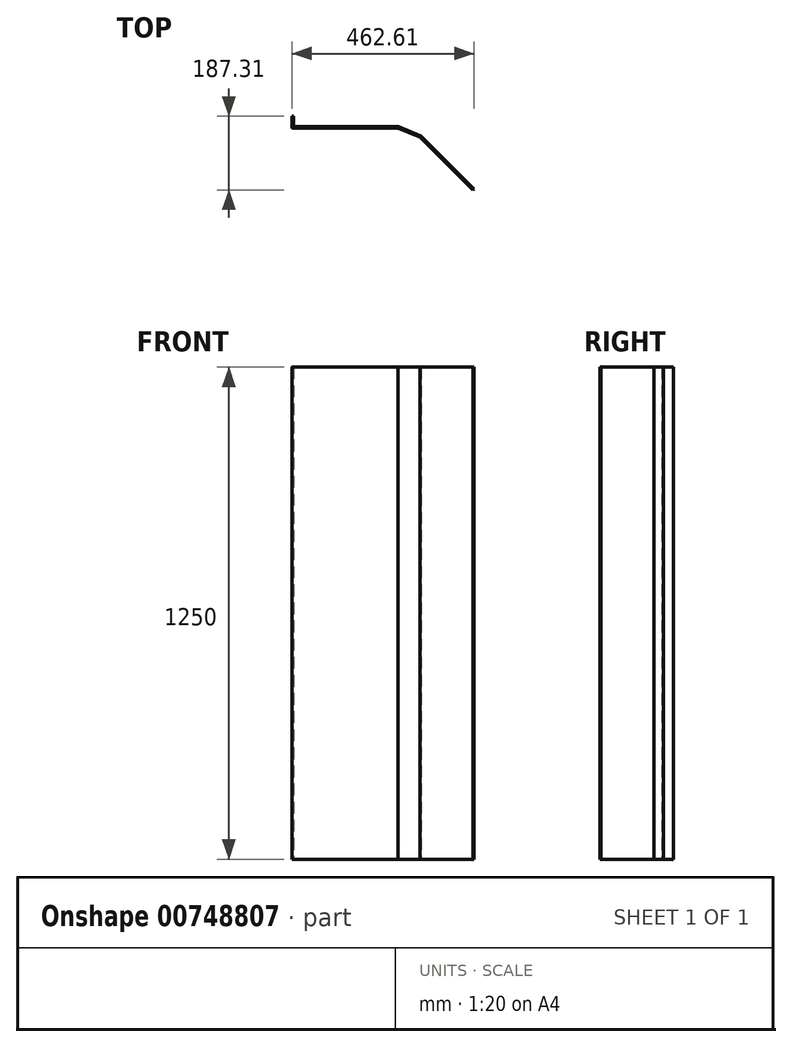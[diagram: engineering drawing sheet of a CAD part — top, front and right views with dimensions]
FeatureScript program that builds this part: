
annotation { "Feature Type Name" : "Feature", "Feature Type Description" : "" }
export const myFeature = defineFeature(function(context is Context, id is Id, definition is map)
    precondition{}
    {
        {
            var Q0;
            Q0=qCreatedBy(makeId("Top.planeOp"),FACE);
            var sketch = newSketch(context, id + "F0", { "sketchPlane" : qUnion([Q0])});
            skLineSegment(sketch, "E0", {"start": v(2, 0) * mm, "end": v(270, 0) * mm});
            skLineSegment(sketch, "E1", {"start": v(270, 0) * mm, "end": v(325.43, -22.96) * mm});
            skLineSegment(sketch, "E2", {"start": v(325.43, -22.96) * mm, "end": v(459.78, -157.31) * mm});
            skLineSegment(sketch, "E3", {"start": v(0, 2) * mm, "end": v(0, 30) * mm});
            skLineSegment(sketch, "E4", {"start": v(0, 30) * mm, "end": v(4, 30) * mm});
            skLineSegment(sketch, "E5", {"start": v(4, 30) * mm, "end": v(4, 6) * mm});
            skLineSegment(sketch, "E6", {"start": v(6, 4) * mm, "end": v(270.8, 4) * mm});
            skLineSegment(sketch, "E7", {"start": v(270.8, 4) * mm, "end": v(327.7, -19.57) * mm});
            skLineSegment(sketch, "E8", {"start": v(327.7, -19.57) * mm, "end": v(462.61, -154.48) * mm});
            skLineSegment(sketch, "E9", {"start": v(459.78, -157.31) * mm, "end": v(462.61, -154.48) * mm});
            skPoint(sketch, "E10.visualSharp", {"position": v(0, 0) * mm});
            skArc(sketch, "E10.filletArc", {"start": v(0, 2) * mm, "mid": v(0.59, 0.59) * mm, "end": v(2, 0) * mm});
            skPoint(sketch, "E11.visualSharp", {"position": v(4, 4) * mm});
            skArc(sketch, "E11.filletArc", {"start": v(4, 6) * mm, "mid": v(4.59, 4.59) * mm, "end": v(6, 4) * mm});
            skSolve(sketch);
        }
        {
            var Q0;
            Q0=makeQuery(id+"F0.imprint","IMPRINT",FACE,{"disambiguationData":[TD([[makeQuery(id+"F0.imprint","IMPRINT",EDGE,{"derivedFrom":sQuery(id+"F0.wireOp",EDGE,"E0")}),1.0]])]});
            extrude(context, id + "F1", {"entities" : qUnion([Q0]), "depth" : 1250 * mm, "offsetDistance" : 25 * mm});
        }
    });
